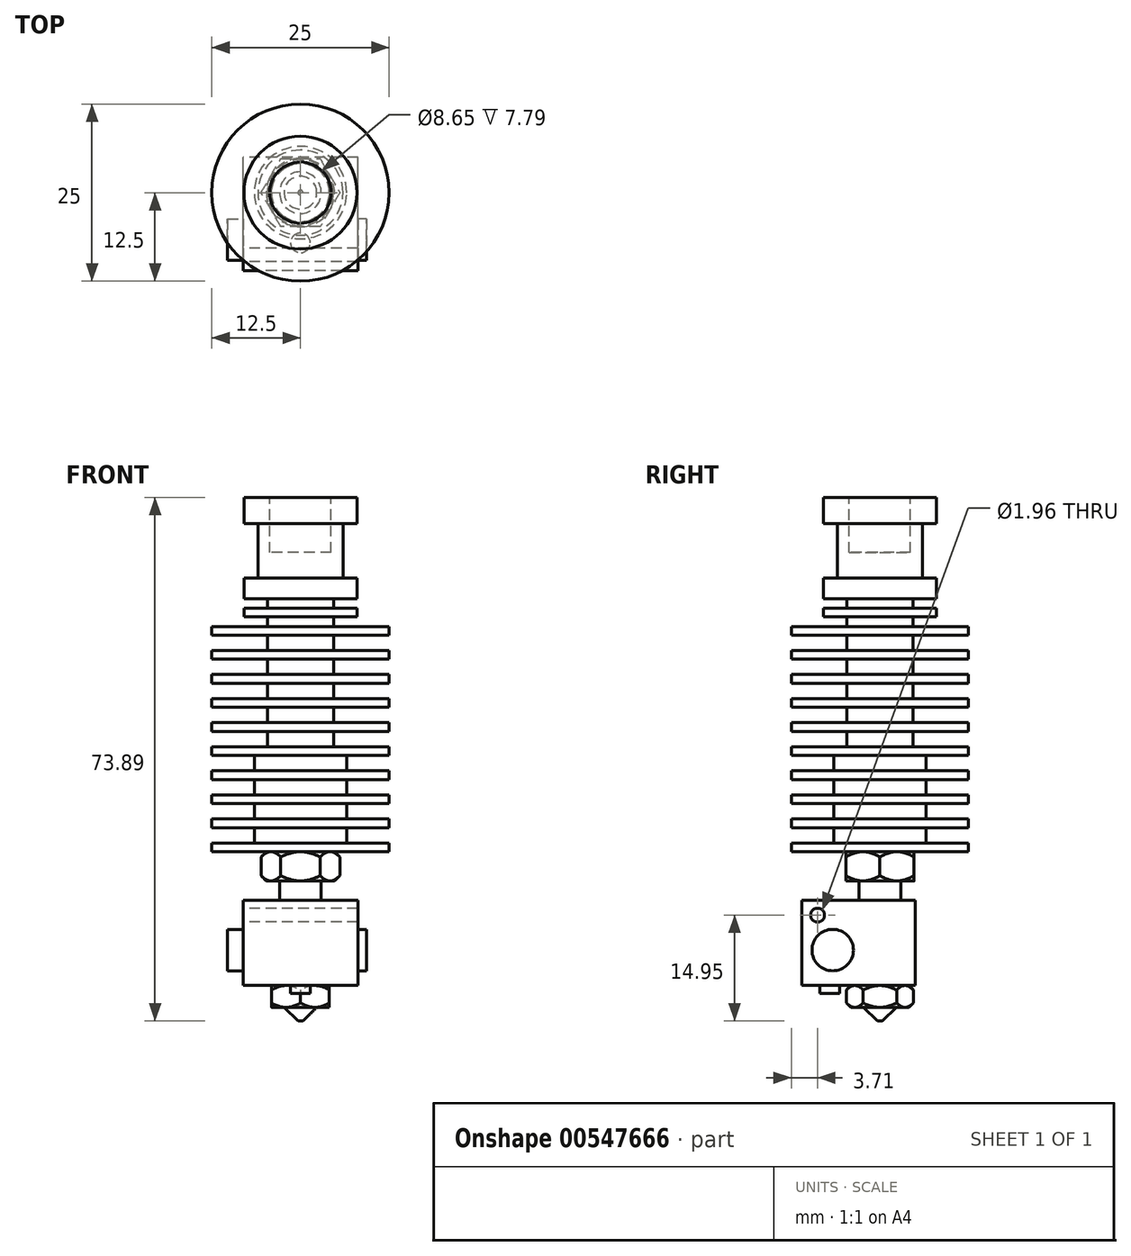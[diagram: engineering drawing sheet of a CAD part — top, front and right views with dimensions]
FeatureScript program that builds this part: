
annotation { "Feature Type Name" : "Feature", "Feature Type Description" : "" }
export const myFeature = defineFeature(function(context is Context, id is Id, definition is map)
    precondition{}
    {
        {
            var Q0;
            Q0=qCreatedBy(makeId("Front.planeOp"),FACE);
            var sketch = newSketch(context, id + "F0", { "sketchPlane" : qUnion([Q0])});
            skLineSegment(sketch, "E0", {"start": v(0, 0) * mm, "end": v(0, -73.89) * mm});
            skLineSegment(sketch, "E1", {"start": v(0, -7.79) * mm, "end": v(-4.32, -7.8) * mm});
            skLineSegment(sketch, "E2", {"start": v(-4.33, 0) * mm, "end": v(-4.33, -7.8) * mm});
            skLineSegment(sketch, "E3", {"start": v(-4.33, 0) * mm, "end": v(-7.97, 0) * mm});
            skLineSegment(sketch, "E4", {"start": v(-7.97, 0) * mm, "end": v(-7.97, -3.67) * mm});
            skLineSegment(sketch, "E5", {"start": v(-7.97, -3.67) * mm, "end": v(-6, -3.67) * mm});
            skLineSegment(sketch, "E6", {"start": v(-6, -3.67) * mm, "end": v(-6, -11.4) * mm});
            skLineSegment(sketch, "E7", {"start": v(-6, -11.4) * mm, "end": v(-7.97, -11.4) * mm});
            skLineSegment(sketch, "E8", {"start": v(-7.97, -11.4) * mm, "end": v(-7.97, -14.3) * mm});
            skLineSegment(sketch, "E9", {"start": v(-7.97, -14.31) * mm, "end": v(-4.66, -14.31) * mm});
            skLineSegment(sketch, "E10", {"start": v(-4.66, -14.31) * mm, "end": v(-4.66, -15.65) * mm});
            skLineSegment(sketch, "E11", {"start": v(-4.66, -16.87) * mm, "end": v(-4.66, -18.21) * mm});
            skLineSegment(sketch, "E12", {"start": v(-4.66, -18.21) * mm, "end": v(-12.5, -18.21) * mm});
            skLineSegment(sketch, "E13", {"start": v(-12.5, -50) * mm, "end": v(-2.94, -50) * mm});
            skLineSegment(sketch, "E14", {"start": v(-2.94, -50) * mm, "end": v(-2.94, -71.96) * mm});
            skLineSegment(sketch, "E15", {"start": v(-2.3, -71.96) * mm, "end": v(-2.94, -71.96) * mm});
            skLineSegment(sketch, "E16", {"start": v(-2.3, -71.96) * mm, "end": v(-0.35, -73.89) * mm});
            skLineSegment(sketch, "E17", {"start": v(-0.35, -73.89) * mm, "end": v(0, -73.89) * mm});
            skLineSegment(sketch, "E18", {"start": v(0, 0) * mm, "end": v(0, -7.79) * mm});
            skLineSegment(sketch, "E19", {"start": v(-4.66, -15.65) * mm, "end": v(-7.97, -15.65) * mm});
            skLineSegment(sketch, "E20", {"start": v(-7.97, -15.65) * mm, "end": v(-7.97, -16.87) * mm});
            skLineSegment(sketch, "E21", {"start": v(-7.97, -16.87) * mm, "end": v(-4.66, -16.87) * mm});
            skCircle(sketch, "E22", {"center": v(-12.5, -19.9) * mm, "radius": 1.7 * mm, "construction": true});
            skLineSegment(sketch, "E23", {"start": v(-12.5, -18.21) * mm, "end": v(-14.2, -18.21) * mm, "construction": true});
            skLineSegment(sketch, "E24", {"start": v(-14.2, -18.21) * mm, "end": v(-14.2, -50) * mm, "construction": true});
            skLineSegment(sketch, "E25", {"start": v(-14.2, -50) * mm, "end": v(-12.5, -50) * mm, "construction": true});
            skCircle(sketch, "E26", {"center": v(-12.5, -23.3) * mm, "radius": 1.7 * mm, "construction": true});
            skCircle(sketch, "E27", {"center": v(-12.5, -26.7) * mm, "radius": 1.7 * mm, "construction": true});
            skCircle(sketch, "E28", {"center": v(-12.5, -30.1) * mm, "radius": 1.7 * mm, "construction": true});
            skCircle(sketch, "E29", {"center": v(-12.5, -33.49) * mm, "radius": 1.7 * mm, "construction": true});
            skCircle(sketch, "E30", {"center": v(-12.5, -36.89) * mm, "radius": 1.7 * mm, "construction": true});
            skCircle(sketch, "E31", {"center": v(-12.5, -40.28) * mm, "radius": 1.7 * mm, "construction": true});
            skCircle(sketch, "E32", {"center": v(-12.5, -43.68) * mm, "radius": 1.7 * mm, "construction": true});
            skLineSegment(sketch, "E33", {"start": v(-12.5, -18.21) * mm, "end": v(-12.5, -50) * mm, "construction": true});
            skCircle(sketch, "E34", {"center": v(-7.97, -16.26) * mm, "radius": 1.95 * mm, "construction": true});
            skLineSegment(sketch, "E35", {"start": v(-12.5, -18.21) * mm, "end": v(-12.5, -19.43) * mm});
            skLineSegment(sketch, "E36", {"start": v(-12.5, -19.43) * mm, "end": v(-4.66, -19.43) * mm});
            skLineSegment(sketch, "E37", {"start": v(-4.66, -19.43) * mm, "end": v(-4.66, -21.6) * mm});
            skLineSegment(sketch, "E38", {"start": v(-4.66, -21.6) * mm, "end": v(-12.5, -21.6) * mm});
            skLineSegment(sketch, "E39", {"start": v(-13.11, -18.21) * mm, "end": v(-13.1, -50) * mm, "construction": true});
            skCircle(sketch, "E40", {"center": v(-12.5, -47.07) * mm, "radius": 1.7 * mm, "construction": true});
            skLineSegment(sketch, "E41", {"start": v(-12.5, -50) * mm, "end": v(-12.5, -48.77) * mm});
            skLineSegment(sketch, "E42", {"start": v(-12.5, -48.77) * mm, "end": v(-6.52, -48.77) * mm});
            skLineSegment(sketch, "E43", {"start": v(-6.52, -48.77) * mm, "end": v(-6.52, -46.6) * mm});
            skCircle(sketch, "E44", {"center": v(-12.5, -49.38) * mm, "radius": 0.61 * mm, "construction": true});
            skCircle(sketch, "E45", {"center": v(-12.5, -18.82) * mm, "radius": 0.61 * mm, "construction": true});
            skCircle(sketch, "E46", {"center": v(-12.5, -22.22) * mm, "radius": 0.61 * mm, "construction": true});
            skCircle(sketch, "E47", {"center": v(-12.5, -25.61) * mm, "radius": 0.61 * mm, "construction": true});
            skCircle(sketch, "E48", {"center": v(-12.5, -29) * mm, "radius": 0.61 * mm, "construction": true});
            skCircle(sketch, "E49", {"center": v(-12.5, -32.4) * mm, "radius": 0.61 * mm, "construction": true});
            skCircle(sketch, "E50", {"center": v(-12.5, -35.8) * mm, "radius": 0.61 * mm, "construction": true});
            skCircle(sketch, "E51", {"center": v(-12.5, -39.2) * mm, "radius": 0.61 * mm, "construction": true});
            skCircle(sketch, "E52", {"center": v(-12.5, -42.59) * mm, "radius": 0.61 * mm, "construction": true});
            skCircle(sketch, "E53", {"center": v(-12.5, -45.98) * mm, "radius": 0.61 * mm, "construction": true});
            skLineSegment(sketch, "E54", {"start": v(-6.52, -46.6) * mm, "end": v(-12.5, -46.6) * mm});
            skLineSegment(sketch, "E55", {"start": v(-12.5, -46.6) * mm, "end": v(-12.5, -45.37) * mm});
            skLineSegment(sketch, "E56", {"start": v(-12.5, -45.37) * mm, "end": v(-6.52, -45.37) * mm});
            skLineSegment(sketch, "E57", {"start": v(-6.52, -45.37) * mm, "end": v(-6.52, -43.2) * mm});
            skLineSegment(sketch, "E58", {"start": v(-6.52, -43.2) * mm, "end": v(-12.5, -43.2) * mm});
            skLineSegment(sketch, "E59", {"start": v(-12.5, -43.2) * mm, "end": v(-12.5, -41.98) * mm});
            skLineSegment(sketch, "E60", {"start": v(-12.5, -41.98) * mm, "end": v(-6.52, -41.98) * mm});
            skLineSegment(sketch, "E61", {"start": v(-12.5, -38.58) * mm, "end": v(-12.5, -39.8) * mm});
            skLineSegment(sketch, "E62", {"start": v(-12.5, -39.8) * mm, "end": v(-6.52, -39.8) * mm});
            skLineSegment(sketch, "E63", {"start": v(-6.52, -39.8) * mm, "end": v(-6.52, -41.98) * mm});
            skLineSegment(sketch, "E64", {"start": v(-12.5, -38.58) * mm, "end": v(-6.52, -38.58) * mm});
            skLineSegment(sketch, "E65", {"start": v(-6.52, -38.58) * mm, "end": v(-6.52, -36.4) * mm});
            skLineSegment(sketch, "E66", {"start": v(-6.52, -36.4) * mm, "end": v(-12.5, -36.4) * mm});
            skLineSegment(sketch, "E67", {"start": v(-12.5, -36.4) * mm, "end": v(-12.5, -35.19) * mm});
            skLineSegment(sketch, "E68", {"start": v(-12.5, -35.19) * mm, "end": v(-4.66, -35.19) * mm});
            skLineSegment(sketch, "E69", {"start": v(-4.66, -35.19) * mm, "end": v(-4.66, -33.01) * mm});
            skLineSegment(sketch, "E70", {"start": v(-4.66, -33.01) * mm, "end": v(-12.5, -33.01) * mm});
            skLineSegment(sketch, "E71", {"start": v(-12.5, -33.01) * mm, "end": v(-12.5, -31.8) * mm});
            skLineSegment(sketch, "E72", {"start": v(-12.5, -21.6) * mm, "end": v(-12.5, -22.83) * mm});
            skLineSegment(sketch, "E73", {"start": v(-12.5, -22.83) * mm, "end": v(-4.66, -22.83) * mm});
            skLineSegment(sketch, "E74", {"start": v(-4.66, -22.83) * mm, "end": v(-4.66, -25) * mm});
            skLineSegment(sketch, "E75", {"start": v(-4.66, -25) * mm, "end": v(-12.5, -25) * mm});
            skLineSegment(sketch, "E76", {"start": v(-12.5, -25) * mm, "end": v(-12.5, -26.22) * mm});
            skLineSegment(sketch, "E77", {"start": v(-12.5, -26.22) * mm, "end": v(-4.66, -26.22) * mm});
            skLineSegment(sketch, "E78", {"start": v(-4.66, -26.22) * mm, "end": v(-4.66, -28.4) * mm});
            skLineSegment(sketch, "E79", {"start": v(-4.66, -28.4) * mm, "end": v(-12.5, -28.4) * mm});
            skLineSegment(sketch, "E80", {"start": v(-12.5, -28.4) * mm, "end": v(-12.5, -29.62) * mm});
            skLineSegment(sketch, "E81", {"start": v(-12.5, -31.8) * mm, "end": v(-4.66, -31.8) * mm});
            skLineSegment(sketch, "E82", {"start": v(-4.66, -31.8) * mm, "end": v(-4.66, -29.62) * mm});
            skLineSegment(sketch, "E83", {"start": v(-4.66, -29.62) * mm, "end": v(-12.5, -29.62) * mm});
            skSolve(sketch);
        }
        {
            var Q0;
            Q0=makeQuery(id+"F0.imprint","IMPRINT",FACE,{"disambiguationData":[TD([[makeQuery(id+"F0.imprint","IMPRINT",EDGE,{"derivedFrom":sQuery(id+"F0.wireOp",EDGE,"E0")}),-1.0]])]});
            var Q1;
            Q1=sQuery(id+"F0.wireOp",EDGE,"E0");
            revolve(context, id + "F1", {"entities" : qUnion([Q0]), "axis" : qUnion([Q1]), "revolveType" : RevolveType.FULL});
        }
        {
            var Q0;
            Q0=makeQuery(id+"F1.opRevolve","SWEPT_FACE",FACE,{"disambiguationData":[OSD([sQuery(id+"F0.wireOp",EDGE,"E15")])]});
            var sketch = newSketch(context, id + "F2", { "sketchPlane" : qUnion([Q0])});
            skCircle(sketch, "E84.cCircle", {"center": v(0, 0) * mm, "radius": 4.08 * mm, "construction": true});
            skLineSegment(sketch, "E84.0", {"start": v(-4.08, -2.36) * mm, "end": v(-4.08, 2.36) * mm});
            skLineSegment(sketch, "E84.1", {"start": v(-4.08, 2.36) * mm, "end": v(0, 4.72) * mm});
            skLineSegment(sketch, "E84.2", {"start": v(0, 4.72) * mm, "end": v(4.08, 2.36) * mm});
            skLineSegment(sketch, "E84.3", {"start": v(4.08, 2.36) * mm, "end": v(4.09, -2.36) * mm});
            skLineSegment(sketch, "E84.4", {"start": v(4.09, -2.36) * mm, "end": v(0, -4.72) * mm});
            skLineSegment(sketch, "E84.5", {"start": v(0, -4.72) * mm, "end": v(-4.08, -2.36) * mm});
            skPoint(sketch, "E84.0.midPoint", {"position": v(-4.08, 0) * mm});
            skSolve(sketch);
        }
        {
            var Q0;
            Q0=qSketchRegion(id+"F2",true);
            extrude(context, id + "F3", {"entities" : qUnion([Q0]), "operationType" : NewBodyOperationType.ADD, "oppositeDirection" : true, "depth" : 3.09 * mm});
        }
        {
            var Q0;
            Q0=qCreatedBy(makeId("Front.planeOp"),FACE);
            var sketch = newSketch(context, id + "F4", { "sketchPlane" : qUnion([Q0])});
            skLineSegment(sketch, "E85.0", {"start": v(-4.08, -68.87) * mm, "end": v(-4.08, -71.96) * mm, "construction": true});
            skLineSegment(sketch, "E86", {"start": v(-4.08, -71.96) * mm, "end": v(-5.63, -70.42) * mm});
            skLineSegment(sketch, "E87", {"start": v(-5.63, -70.42) * mm, "end": v(-4.09, -68.87) * mm});
            skLineSegment(sketch, "E88", {"start": v(-5.63, -70.42) * mm, "end": v(-4.08, -70.42) * mm, "construction": true});
            skLineSegment(sketch, "E89", {"start": v(0, -68.87) * mm, "end": v(0, -76.05) * mm, "construction": true});
            skLineSegment(sketch, "E90", {"start": v(0, -76.05) * mm, "end": v(-4.08, -71.96) * mm, "construction": true});
            skLineSegment(sketch, "E91", {"start": v(-4.08, -71.96) * mm, "end": v(-4.08, -72.96) * mm});
            skLineSegment(sketch, "E92", {"start": v(-4.08, -72.96) * mm, "end": v(-7.09, -72.96) * mm});
            skLineSegment(sketch, "E93", {"start": v(-7.08, -72.96) * mm, "end": v(-7.08, -67.87) * mm});
            skLineSegment(sketch, "E94", {"start": v(-7.09, -67.87) * mm, "end": v(-4.08, -67.87) * mm});
            skLineSegment(sketch, "E95", {"start": v(-4.08, -67.87) * mm, "end": v(-4.08, -68.87) * mm});
            skSolve(sketch);
        }
        {
            var Q0;
            Q0=qSketchRegion(id+"F4",true);
            var Q1;
            Q1=sQuery(id+"F4.wireOp",EDGE,"E89");
            revolve(context, id + "F5", {"operationType" : NewBodyOperationType.REMOVE, "entities" : qUnion([Q0]), "axis" : qUnion([Q1]), "revolveType" : RevolveType.FULL, "oppositeDirection" : true});
        }
        {
            var Q0;
            Q0=makeQuery(id+"F3.opExtrude","CAP_FACE",FACE,{"disambiguationData":[OSD([sQuery(id+"F2.wireOp",EDGE,"E84.0"),sQuery(id+"F2.wireOp",EDGE,"E84.1"),sQuery(id+"F2.wireOp",EDGE,"E84.2"),sQuery(id+"F2.wireOp",EDGE,"E84.3"),sQuery(id+"F2.wireOp",EDGE,"E84.4"),sQuery(id+"F2.wireOp",EDGE,"E84.5")])],"isStart":false});
            var sketch = newSketch(context, id + "F6", { "sketchPlane" : qUnion([Q0])});
            skLineSegment(sketch, "E96", {"start": v(0, -11.04) * mm, "end": v(-8.1, -11.04) * mm});
            skLineSegment(sketch, "E97", {"start": v(-8.1, -11.04) * mm, "end": v(-8.1, 4.98) * mm});
            skLineSegment(sketch, "E98", {"start": v(-8.1, 4.98) * mm, "end": v(0, 4.98) * mm});
            skLineSegment(sketch, "E99", {"start": v(0, 4.98) * mm, "end": v(0, 0) * mm, "construction": true});
            skLineSegment(sketch, "E100", {"start": v(0, 0) * mm, "end": v(0, -11.04) * mm, "construction": true});
            skLineSegment(sketch, "E101", {"start": v(0, 4.98) * mm, "end": v(0, 12.5) * mm, "construction": true});
            skCircle(sketch, "E102.0", {"center": v(0, 0) * mm, "radius": 12.5 * mm, "construction": true});
            skLineSegment(sketch, "E103.MirrorCS", {"start": v(0, -11.04) * mm, "end": v(8.1, -11.04) * mm});
            skLineSegment(sketch, "E104.MirrorCS", {"start": v(8.1, -11.04) * mm, "end": v(8.1, 4.98) * mm});
            skLineSegment(sketch, "E105.MirrorCS", {"start": v(8.1, 4.98) * mm, "end": v(0, 4.98) * mm});
            skSolve(sketch);
        }
        {
            var Q0;
            Q0=qSketchRegion(id+"F6",true);
            extrude(context, id + "F7", {"entities" : qUnion([Q0]), "operationType" : NewBodyOperationType.ADD, "depth" : 12.02 * mm});
        }
        {
            var Q0;
            Q0=makeQuery(id+"F7.opExtrude","SWEPT_FACE",FACE,{"disambiguationData":[OSD([sQuery(id+"F6.wireOp",EDGE,"E97")])]});
            var sketch = newSketch(context, id + "F8", { "sketchPlane" : qUnion([Q0])});
            skCircle(sketch, "E106", {"center": v(6.65, -63.88) * mm, "radius": 2.92 * mm});
            skCircle(sketch, "E107", {"center": v(8.79, -58.94) * mm, "radius": 0.98 * mm});
            skSolve(sketch);
        }
        {
            var Q0;
            Q0=makeQuery(id+"F8.imprint","IMPRINT",FACE,{"disambiguationData":[TD([[makeQuery(id+"F8.imprint","IMPRINT",EDGE,{"derivedFrom":sQuery(id+"F8.wireOp",EDGE,"E107")}),1.0]])]});
            extrude(context, id + "F9", {"entities" : qUnion([Q0]), "operationType" : NewBodyOperationType.REMOVE, "endBound" : BoundingType.THROUGH_ALL, "oppositeDirection" : true, "depth" : 25 * mm});
        }
        {
            var Q0;
            Q0=makeQuery(id+"F8.imprint","IMPRINT",FACE,{"disambiguationData":[TD([[makeQuery(id+"F8.imprint","IMPRINT",EDGE,{"derivedFrom":sQuery(id+"F8.wireOp",EDGE,"E106")}),1.0]])]});
            extrude(context, id + "F10", {"entities" : qUnion([Q0]), "operationType" : NewBodyOperationType.ADD, "depth" : 2.17 * mm});
        }
        {
            var Q0;
            Q0=makeQuery(id+"F10.opExtrude","CAP_FACE",FACE,{"disambiguationData":[OSD([sQuery(id+"F8.wireOp",EDGE,"E106")])],"isStart":false});
            extrude(context, id + "F11", {"entities" : qUnion([Q0]), "operationType" : NewBodyOperationType.ADD, "oppositeDirection" : true, "depth" : 19.62 * mm});
        }
        {
            var Q0;
            Q0=makeQuery(id+"F7.opExtrude","CAP_FACE",FACE,{"disambiguationData":[OSD([sQuery(id+"F6.wireOp",EDGE,"E96"),sQuery(id+"F6.wireOp",EDGE,"E97"),sQuery(id+"F6.wireOp",EDGE,"E98"),sQuery(id+"F6.wireOp",EDGE,"E103.MirrorCS"),sQuery(id+"F6.wireOp",EDGE,"E104.MirrorCS"),sQuery(id+"F6.wireOp",EDGE,"E105.MirrorCS")])],"isStart":true});
            var sketch = newSketch(context, id + "F12", { "sketchPlane" : qUnion([Q0])});
            skLineSegment(sketch, "E108", {"start": v(0, 0) * mm, "end": v(0, 11.04) * mm, "construction": true});
            skCircle(sketch, "E109", {"center": v(0, 7.08) * mm, "radius": 1.39 * mm});
            skSolve(sketch);
        }
        {
            var Q0;
            Q0=qSketchRegion(id+"F12",true);
            extrude(context, id + "F13", {"entities" : qUnion([Q0]), "operationType" : NewBodyOperationType.ADD, "depth" : 1.12 * mm});
        }
        {
            var Q0;
            Q0=makeQuery(id+"F1.opRevolve","SWEPT_FACE",FACE,{"disambiguationData":[OSD([sQuery(id+"F0.wireOp",EDGE,"E13")])]});
            var sketch = newSketch(context, id + "F14", { "sketchPlane" : qUnion([Q0])});
            skCircle(sketch, "E110.cCircle", {"center": v(0, 0) * mm, "radius": 4.8 * mm, "construction": true});
            skLineSegment(sketch, "E110.0", {"start": v(-2.78, 4.8) * mm, "end": v(2.78, 4.8) * mm});
            skLineSegment(sketch, "E110.1", {"start": v(2.78, 4.81) * mm, "end": v(5.55, 0) * mm});
            skLineSegment(sketch, "E110.2", {"start": v(5.55, 0) * mm, "end": v(2.78, -4.8) * mm});
            skLineSegment(sketch, "E110.3", {"start": v(2.78, -4.8) * mm, "end": v(-2.78, -4.81) * mm});
            skLineSegment(sketch, "E110.4", {"start": v(-2.78, -4.81) * mm, "end": v(-5.55, 0) * mm});
            skLineSegment(sketch, "E110.5", {"start": v(-5.55, 0) * mm, "end": v(-2.78, 4.8) * mm});
            skPoint(sketch, "E110.0.midPoint", {"position": v(0, 4.8) * mm});
            skSolve(sketch);
        }
        {
            var Q0;
            Q0=qSketchRegion(id+"F14",true);
            extrude(context, id + "F15", {"entities" : qUnion([Q0]), "operationType" : NewBodyOperationType.ADD, "depth" : 4.13 * mm});
        }
        {
            var Q0;
            Q0=qCreatedBy(makeId("Right.planeOp"),FACE);
            var sketch = newSketch(context, id + "F16", { "sketchPlane" : qUnion([Q0])});
            skLineSegment(sketch, "E111", {"start": v(0, 0) * mm, "end": v(0, -58.93) * mm, "construction": true});
            skLineSegment(sketch, "E112", {"start": v(0, -58.93) * mm, "end": v(6.88, -52.06) * mm});
            skLineSegment(sketch, "E113", {"start": v(6.88, -52.06) * mm, "end": v(4.81, -50) * mm});
            skLineSegment(sketch, "E114.0", {"start": v(4.81, -54.12) * mm, "end": v(4.81, -50) * mm, "construction": true});
            skLineSegment(sketch, "E115", {"start": v(4.81, -52.06) * mm, "end": v(6.88, -52.06) * mm, "construction": true});
            skLineSegment(sketch, "E116", {"start": v(4.81, -50) * mm, "end": v(8.81, -50) * mm});
            skLineSegment(sketch, "E117", {"start": v(8.81, -50) * mm, "end": v(8.81, -54.12) * mm});
            skLineSegment(sketch, "E118", {"start": v(8.81, -54.12) * mm, "end": v(4.81, -54.12) * mm});
            skSolve(sketch);
        }
        {
            var Q0;
            Q0=qSketchRegion(id+"F16",true);
            var Q1;
            Q1=sQuery(id+"F16.wireOp",EDGE,"E111");
            revolve(context, id + "F17", {"operationType" : NewBodyOperationType.REMOVE, "entities" : qUnion([Q0]), "axis" : qUnion([Q1]), "revolveType" : RevolveType.FULL, "oppositeDirection" : true});
        }
    });
